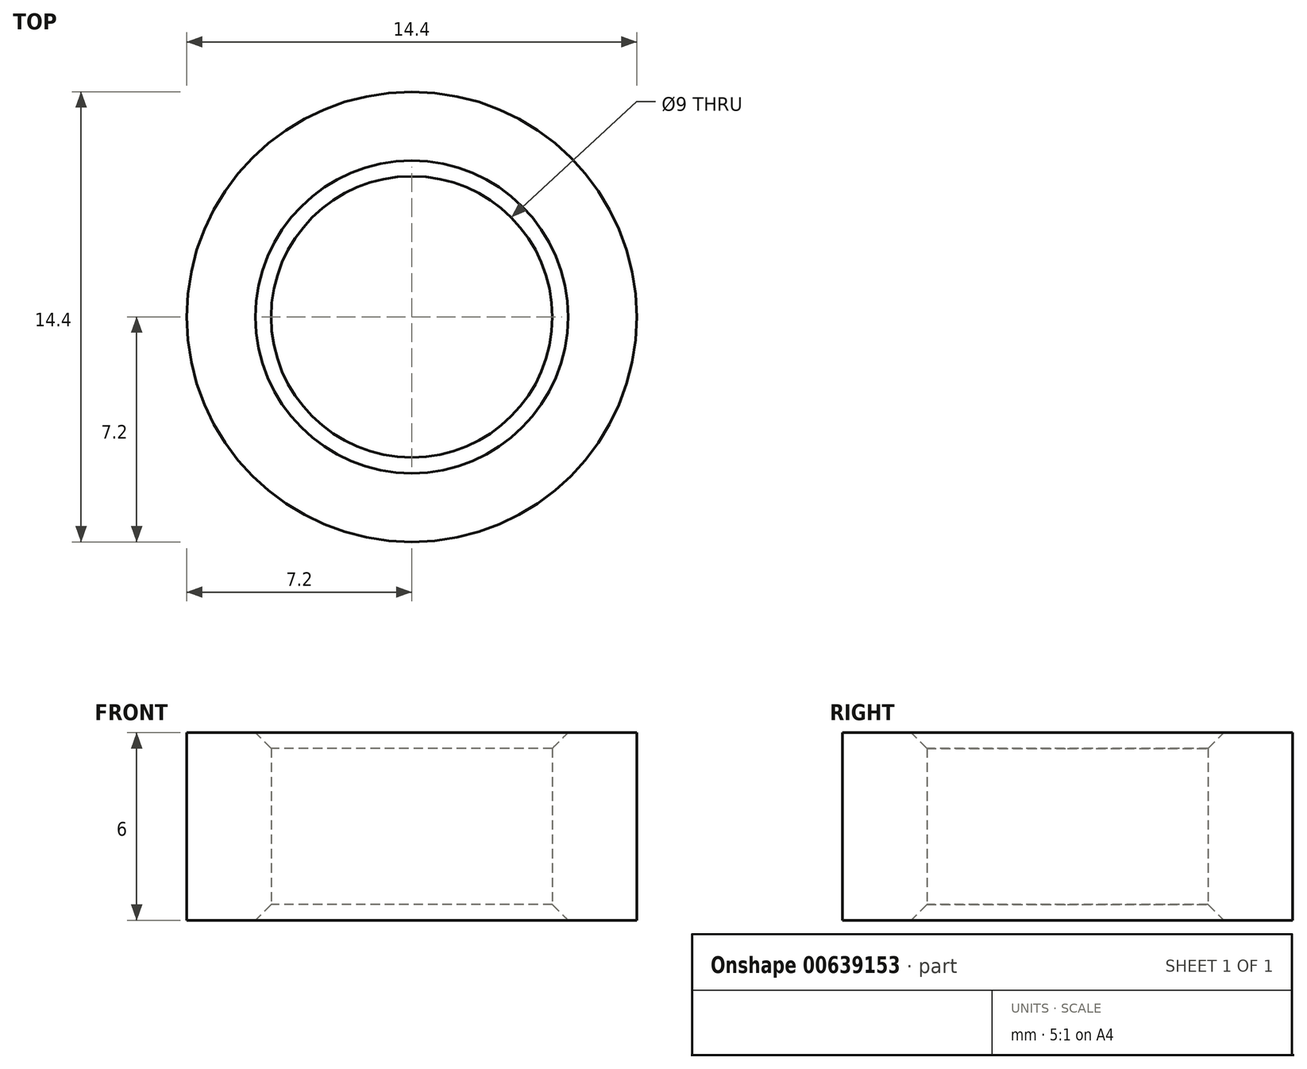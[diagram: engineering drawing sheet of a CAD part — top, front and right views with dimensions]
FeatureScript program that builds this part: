
annotation { "Feature Type Name" : "Feature", "Feature Type Description" : "" }
export const myFeature = defineFeature(function(context is Context, id is Id, definition is map)
    precondition{}
    {
        {
            var Q0;
            Q0=qCreatedBy(makeId("Top.planeOp"),FACE);
            var sketch = newSketch(context, id + "F0", { "sketchPlane" : qUnion([Q0])});
            skCircle(sketch, "E0", {"center": v(0, 0) * mm, "radius": 7.2 * mm});
            skCircle(sketch, "E1", {"center": v(0, 0) * mm, "radius": 4.5 * mm});
            skSolve(sketch);
        }
        {
            var Q0;
            Q0=makeQuery(id+"F0.imprint","IMPRINT",FACE,{"disambiguationData":[TD([[makeQuery(id+"F0.imprint","IMPRINT",EDGE,{"derivedFrom":sQuery(id+"F0.wireOp",EDGE,"E0")}),1.0]])]});
            extrude(context, id + "F1", {"entities" : qUnion([Q0]), "depth" : 6 * mm, "offsetDistance" : 25.4 * mm});
        }
        {
            var Q0;
            Q0=makeQuery(id+"F1.opExtrude","CAP_EDGE",EDGE,{"disambiguationData":[OSD([sQuery(id+"F0.wireOp",EDGE,"E1")])],"isStart":false});
            chamfer(context, id + "F2", {"entities" : qUnion([Q0]), "chamferType" : ChamferType.OFFSET_ANGLE, "width" : 0.5 * mm, "oppositeDirection" : false, "angle" : 45 * degree, "tangentPropagation" : true});
        }
        {
            var Q0;
            Q0=makeQuery(id+"F1.opExtrude","CAP_EDGE",EDGE,{"disambiguationData":[OSD([sQuery(id+"F0.wireOp",EDGE,"E1")])],"isStart":true});
            chamfer(context, id + "F3", {"entities" : qUnion([Q0]), "chamferType" : ChamferType.OFFSET_ANGLE, "width" : 0.5 * mm, "oppositeDirection" : false, "angle" : 45 * degree, "tangentPropagation" : true});
        }
    });
